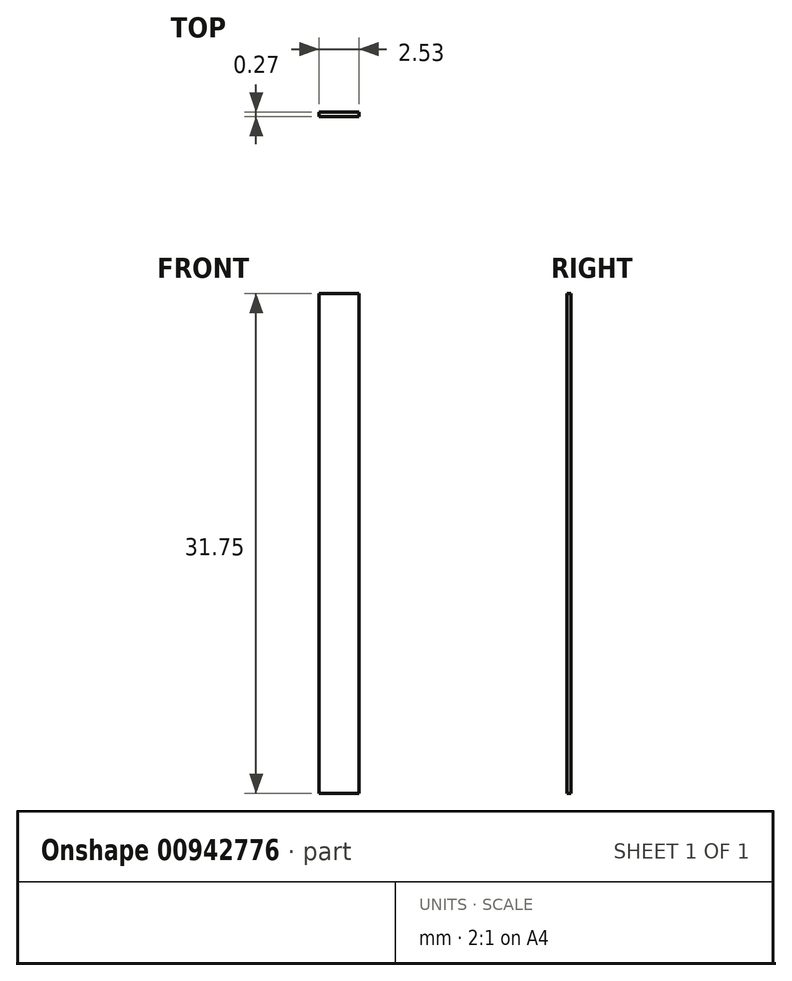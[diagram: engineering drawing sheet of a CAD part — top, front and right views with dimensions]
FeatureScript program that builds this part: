
annotation { "Feature Type Name" : "Feature", "Feature Type Description" : "" }
export const myFeature = defineFeature(function(context is Context, id is Id, definition is map)
    precondition{}
    {
        {
            var Q0;
            Q0=qCreatedBy(makeId("Top.planeOp"),FACE);
            var sketch = newSketch(context, id + "F0", { "sketchPlane" : qUnion([Q0])});
            skLineSegment(sketch, "E0.bottom", {"start": v(0, 0) * mm, "end": v(2.53, 0) * mm});
            skLineSegment(sketch, "E0.top", {"start": v(0, 0.27) * mm, "end": v(2.53, 0.27) * mm});
            skLineSegment(sketch, "E0.left", {"start": v(0, 0) * mm, "end": v(0, 0.27) * mm});
            skLineSegment(sketch, "E0.right", {"start": v(2.53, 0) * mm, "end": v(2.53, 0.27) * mm});
            skSolve(sketch);
        }
        {
            var Q0;
            Q0 = qSketchRegion(id + "F0", true);
            extrude(context, id + "F1", {"entities" : qUnion([Q0]), "depth" : 31.75 * mm, "offsetDistance" : 25.4 * mm});
        }
    });
